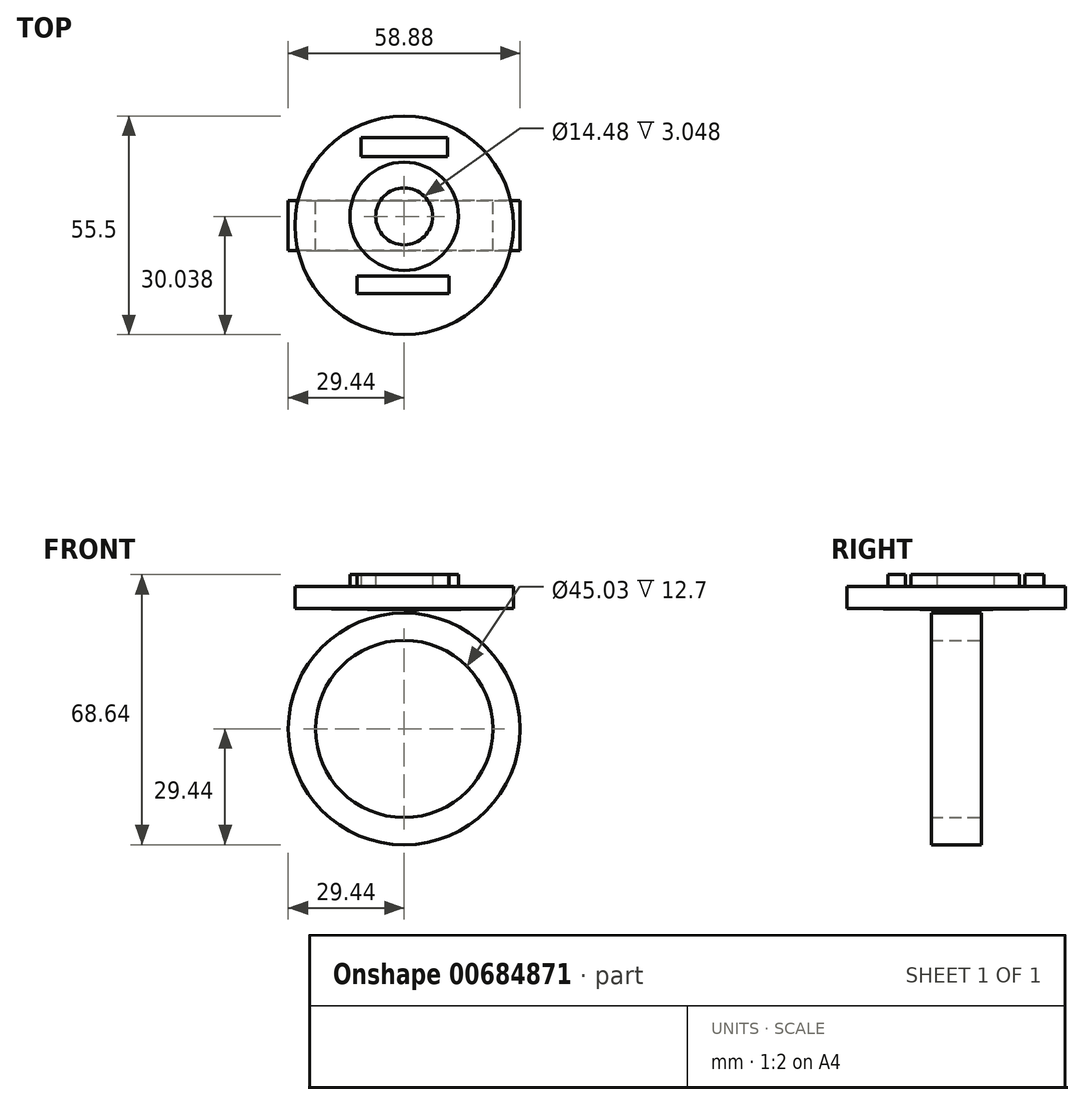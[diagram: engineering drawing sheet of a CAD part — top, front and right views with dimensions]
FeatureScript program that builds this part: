
annotation { "Feature Type Name" : "Feature", "Feature Type Description" : "" }
export const myFeature = defineFeature(function(context is Context, id is Id, definition is map)
    precondition{}
    {
        {
            var Q0;
            Q0=qCreatedBy(makeId("Front.planeOp"),FACE);
            var sketch = newSketch(context, id + "F0", { "sketchPlane" : qUnion([Q0])});
            skCircle(sketch, "E0", {"center": v(0, 0) * mm, "radius": 22.52 * mm});
            skCircle(sketch, "E1", {"center": v(0, 0) * mm, "radius": 29.44 * mm});
            skSolve(sketch);
        }
        {
            var Q0;
            Q0=makeQuery(id+"F0.imprint","IMPRINT",FACE,{"disambiguationData":[TD([[makeQuery(id+"F0.imprint","IMPRINT",EDGE,{"derivedFrom":sQuery(id+"F0.wireOp",EDGE,"E0")}),-1.0]])]});
            extrude(context, id + "F1", {"entities" : qUnion([Q0]), "endBound" : BoundingType.SYMMETRIC, "depth" : 12.7 * mm, "offsetDistance" : 25.4 * mm});
        }
        {
            var Q0;
            Q0=qCreatedBy(makeId("Front.planeOp"),FACE);
            var sketch = newSketch(context, id + "F2", { "sketchPlane" : qUnion([Q0])});
            skLineSegment(sketch, "E2", {"start": v(0, 30.23) * mm, "end": v(0, 36.15) * mm});
            skLineSegment(sketch, "E3", {"start": v(0, 36.15) * mm, "end": v(27.75, 36.15) * mm});
            skLineSegment(sketch, "E4", {"start": v(27.75, 36.15) * mm, "end": v(27.75, 30.58) * mm});
            skLineSegment(sketch, "E5", {"start": v(27.75, 30.58) * mm, "end": v(0, 30.23) * mm});
            skSolve(sketch);
        }
        {
            var Q0;
            Q0=makeQuery(id+"F2.imprint","IMPRINT",FACE,{"disambiguationData":[TD([[makeQuery(id+"F2.imprint","IMPRINT",EDGE,{"derivedFrom":sQuery(id+"F2.wireOp",EDGE,"E2")}),-1.0]])]});
            var Q1;
            Q1=sQuery(id+"F2.wireOp",EDGE,"E2");
            revolve(context, id + "F3", {"entities" : qUnion([Q0]), "axis" : qUnion([Q1]), "revolveType" : RevolveType.FULL});
        }
        {
            var Q0;
            Q0=makeQuery(id+"F3.opRevolve","SWEPT_FACE",FACE,{"disambiguationData":[OSD([sQuery(id+"F2.wireOp",EDGE,"E3")])]});
            var sketch = newSketch(context, id + "F4", { "sketchPlane" : qUnion([Q0])});
            skLineSegment(sketch, "E6.bottom", {"start": v(11.37, -17.35) * mm, "end": v(-11.95, -17.35) * mm});
            skLineSegment(sketch, "E6.top", {"start": v(11.37, -12.87) * mm, "end": v(-11.95, -12.87) * mm});
            skLineSegment(sketch, "E6.left", {"start": v(11.37, -17.35) * mm, "end": v(11.37, -12.87) * mm});
            skLineSegment(sketch, "E6.right", {"start": v(-11.95, -17.35) * mm, "end": v(-11.95, -12.87) * mm});
            skCircle(sketch, "E7", {"center": v(0, 2.29) * mm, "radius": 7.24 * mm});
            skCircle(sketch, "E8", {"center": v(0, 2.29) * mm, "radius": 13.78 * mm});
            skLineSegment(sketch, "E9.bottom", {"start": v(11, 17.41) * mm, "end": v(-10.94, 17.41) * mm});
            skLineSegment(sketch, "E9.top", {"start": v(11, 22.25) * mm, "end": v(-10.94, 22.25) * mm});
            skLineSegment(sketch, "E9.left", {"start": v(11, 17.41) * mm, "end": v(11, 22.25) * mm});
            skLineSegment(sketch, "E9.right", {"start": v(-10.94, 17.41) * mm, "end": v(-10.94, 22.25) * mm});
            skSolve(sketch);
        }
        {
            var Q0;
            Q0=makeQuery(id+"F4.imprint","IMPRINT",FACE,{"disambiguationData":[TD([[makeQuery(id+"F4.imprint","IMPRINT",EDGE,{"derivedFrom":sQuery(id+"F4.wireOp",EDGE,"E6.bottom")}),-1.0]])]});
            var Q1;
            Q1=makeQuery(id+"F4.imprint","IMPRINT",FACE,{"disambiguationData":[TD([[makeQuery(id+"F4.imprint","IMPRINT",EDGE,{"derivedFrom":sQuery(id+"F4.wireOp",EDGE,"E7")}),-1.0]])]});
            var Q2;
            Q2=makeQuery(id+"F4.imprint","IMPRINT",FACE,{"disambiguationData":[TD([[makeQuery(id+"F4.imprint","IMPRINT",EDGE,{"derivedFrom":sQuery(id+"F4.wireOp",EDGE,"E9.bottom")}),-1.0]])]});
            extrude(context, id + "F5", {"entities" : qUnion([Q0, Q1, Q2]), "operationType" : NewBodyOperationType.ADD, "depth" : 3.05 * mm, "offsetDistance" : 25.4 * mm});
        }
    });
